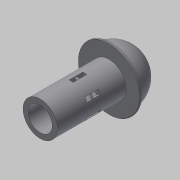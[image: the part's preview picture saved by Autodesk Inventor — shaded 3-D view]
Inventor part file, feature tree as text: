
AUTODESK INVENTOR PART (.ipt)
format: ipt  version: 2018 (Build 220112000, 112)  size: 321,536 bytes
history: native  units: mm
features: sketch x12, other x7, extrude x7, projected_geometry x4, fillet x3, pattern_circular x2
ambient origin geometry x8: Origin, YZ Plane, XZ Plane, XY Plane, X Axis, Y Axis, Z Axis, Center Point
bodies: Body1 (feature_tree)
feature tree (35):
  other  "實體1"
  other  "迴轉1"
  other  "迴轉2"
  fillet  "圓角1"  Radius=100.0mm
  fillet  "圓角2"  Radius=25.0mm
  other  "迴轉3"
  extrude  "擠出1"  TaperAngle=90.0deg  [1 undecoded]
  extrude  "擠出2"  Depth=5.0mm
  pattern_circular  "環形陣列1"  [2 undecoded]
  extrude  "擠出3"  TaperAngle=90.0deg  [1 undecoded]
  fillet  "圓角3"  Radius=3.0mm
  other  "迴轉4"
  extrude  "擠出4"  Depth=0.5mm
  pattern_circular  "環形陣列2"  Angle=90.0deg  [1 undecoded]
  sketch  "草圖9"
  other  "刪除面1"
  extrude  "擠出5"  Depth=35.0mm
  extrude  "擠出6"  Depth=40.0mm TaperAngle=0.0deg
  extrude  "擠出7"  Depth=6.0mm
  sketch  "草圖1"
  sketch  "草圖2"
  sketch  "草圖3"
  sketch  "草圖4"
  sketch  "草圖5"
  projected_geometry  "投影迴路1"
  sketch  "草圖6"
  sketch  "草圖7"
  sketch  "草圖8"
  projected_geometry  "投影迴路2"
  projected_geometry  "投影迴路3"
  sketch  "草圖10"
  sketch  "草圖11"
  projected_geometry  "投影迴路4"
  sketch  "草圖12"
  other  "投影切割邊1"
note: 5 required parameter values undecoded (feature->parameter linkage not recoverable at this tier; creation-order binding heuristic only, values carry confidence <= 0.55)
